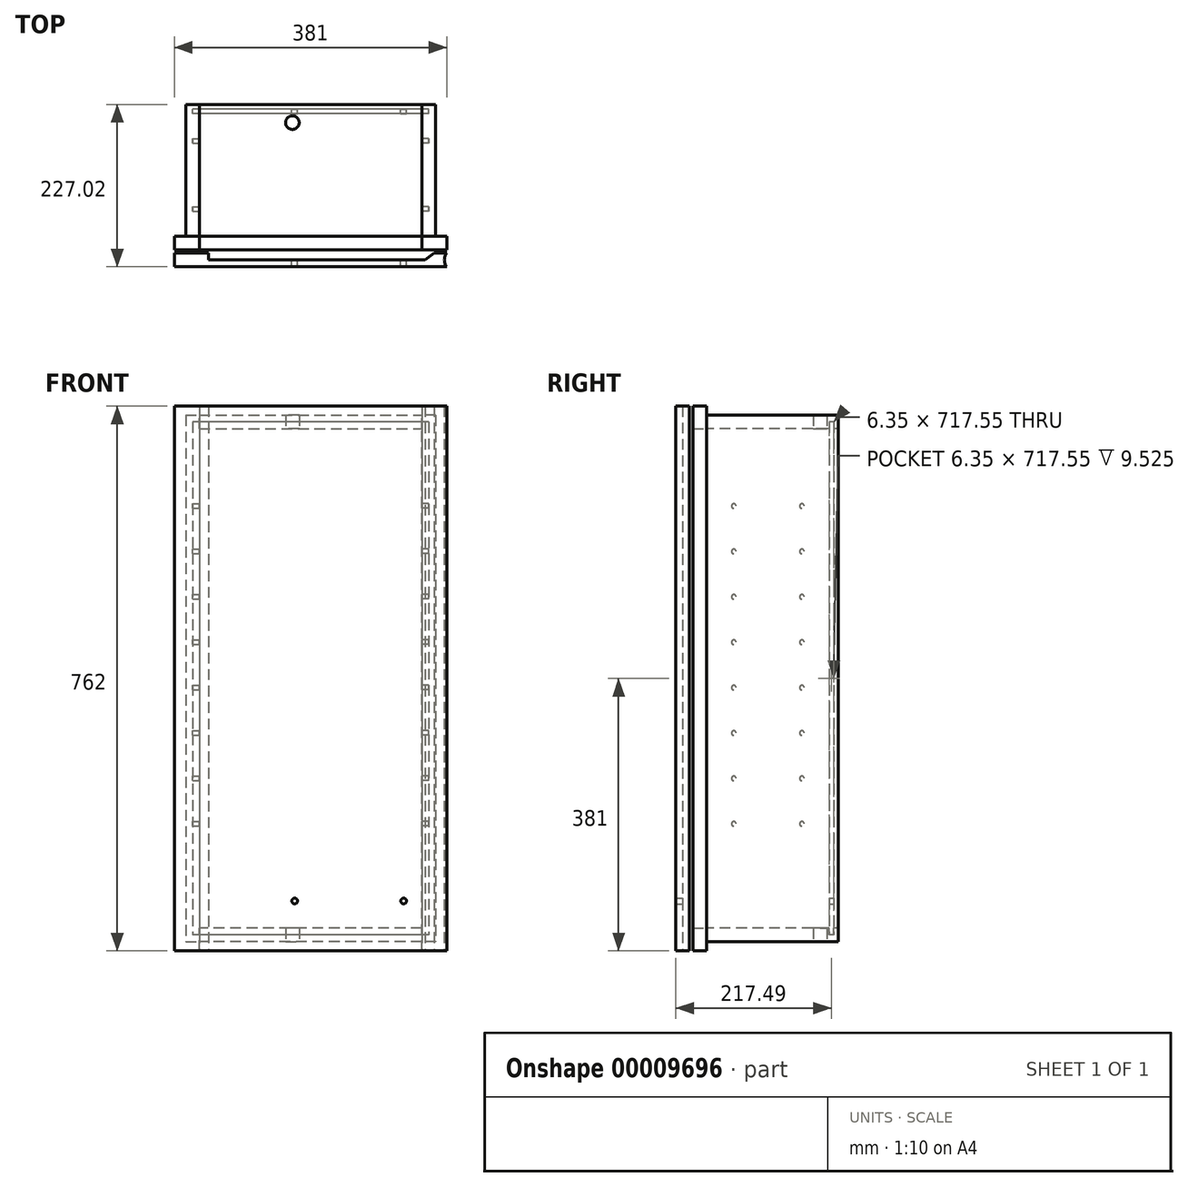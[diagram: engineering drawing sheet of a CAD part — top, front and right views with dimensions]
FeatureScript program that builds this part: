
annotation { "Feature Type Name" : "Feature", "Feature Type Description" : "" }
export const myFeature = defineFeature(function(context is Context, id is Id, definition is map)
    precondition{}
    {
        {
            var Q0;
            Q0=qCreatedBy(makeId("Top.planeOp"),FACE);
            var sketch = newSketch(context, id + "F0", { "sketchPlane" : qUnion([Q0])});
            skLineSegment(sketch, "E0.rect.bottom", {"start": v(155.58, 92.08) * mm, "end": v(-155.58, 92.08) * mm});
            skLineSegment(sketch, "E0.rect.top", {"start": v(155.58, -92.08) * mm, "end": v(-155.58, -92.08) * mm});
            skLineSegment(sketch, "E0.rect.left", {"start": v(155.58, 92.08) * mm, "end": v(155.58, -92.07) * mm});
            skLineSegment(sketch, "E0.rect.right", {"start": v(-155.58, 92.07) * mm, "end": v(-155.58, -92.08) * mm});
            skPoint(sketch, "E0.rect.middle", {"position": v(0, 0) * mm});
            skSolve(sketch);
        }
        {
            var Q0;
            Q0=makeQuery(id+"F0.imprint","IMPRINT",FACE,{"disambiguationData":[TD([[makeQuery(id+"F0.imprint","IMPRINT",EDGE,{"derivedFrom":sQuery(id+"F0.wireOp",EDGE,"E0.rect.bottom")}),1.0]])]});
            extrude(context, id + "F1", {"entities" : qUnion([Q0]), "depth" : 19.05 * mm});
        }
        {
            var Q0;
            Q0=makeQuery(id+"F1.opExtrude","SWEPT_FACE",FACE,{"disambiguationData":[OSD([sQuery(id+"F0.wireOp",EDGE,"E0.rect.right")])]});
            var sketch = newSketch(context, id + "F2", { "sketchPlane" : qUnion([Q0])});
            skLineSegment(sketch, "E1.bottom", {"start": v(-92.07, 0) * mm, "end": v(92.08, 0) * mm});
            skLineSegment(sketch, "E1.top", {"start": v(-92.08, 736.6) * mm, "end": v(92.07, 736.6) * mm});
            skLineSegment(sketch, "E1.left", {"start": v(-92.07, 0) * mm, "end": v(-92.08, 736.6) * mm});
            skLineSegment(sketch, "E1.right", {"start": v(92.08, 0) * mm, "end": v(92.07, 736.6) * mm});
            skSolve(sketch);
        }
        {
            var Q0;
            Q0 = qSketchRegion(id + "F2", true);
            extrude(context, id + "F3", {"entities" : qUnion([Q0]), "depth" : 19.05 * mm});
        }
        {
            var Q0;
            Q0=makeQuery(id+"F3.opExtrude","CAP_FACE",FACE,{"disambiguationData":[OSD([sQuery(id+"F2.wireOp",EDGE,"E1.bottom"),sQuery(id+"F2.wireOp",EDGE,"E1.top"),sQuery(id+"F2.wireOp",EDGE,"E1.left"),sQuery(id+"F2.wireOp",EDGE,"E1.right")])],"isStart":true});
            var sketch = newSketch(context, id + "F4", { "sketchPlane" : qUnion([Q0])});
            skCircle(sketch, "E2", {"center": v(-53.98, 165.1) * mm, "radius": 3.18 * mm});
            skCircle(sketch, "E3", {"center": v(41.27, 165.1) * mm, "radius": 3.18 * mm});
            skLineSegment(sketch, "E4", {"start": v(-53.98, 165.1) * mm, "end": v(41.27, 165.1) * mm, "construction": true});
            skCircle(sketch, "E5.0.1.0", {"center": v(-53.98, 228.6) * mm, "radius": 3.18 * mm});
            skCircle(sketch, "E5.0.1.1", {"center": v(41.27, 228.6) * mm, "radius": 3.18 * mm});
            skCircle(sketch, "E5.0.2.0", {"center": v(-53.98, 292.1) * mm, "radius": 3.18 * mm});
            skCircle(sketch, "E5.0.2.1", {"center": v(41.27, 292.1) * mm, "radius": 3.18 * mm});
            skCircle(sketch, "E5.0.3.0", {"center": v(-53.98, 355.6) * mm, "radius": 3.18 * mm});
            skCircle(sketch, "E5.0.3.1", {"center": v(41.27, 355.6) * mm, "radius": 3.18 * mm});
            skCircle(sketch, "E5.0.4.0", {"center": v(-53.98, 419.1) * mm, "radius": 3.18 * mm});
            skCircle(sketch, "E5.0.4.1", {"center": v(41.27, 419.1) * mm, "radius": 3.18 * mm});
            skCircle(sketch, "E5.0.5.0", {"center": v(-53.98, 482.6) * mm, "radius": 3.18 * mm});
            skCircle(sketch, "E5.0.5.1", {"center": v(41.27, 482.6) * mm, "radius": 3.18 * mm});
            skCircle(sketch, "E5.0.6.0", {"center": v(-53.98, 546.1) * mm, "radius": 3.18 * mm});
            skCircle(sketch, "E5.0.6.1", {"center": v(41.27, 546.1) * mm, "radius": 3.18 * mm});
            skLineSegment(sketch, "E5.direction1", {"start": v(-53.98, 165.1) * mm, "end": v(-25.4, 165.1) * mm, "construction": true});
            skLineSegment(sketch, "E5.direction2", {"start": v(-53.98, 165.1) * mm, "end": v(-53.98, 228.6) * mm, "construction": true});
            skCircle(sketch, "E6.0.0.7", {"center": v(-53.98, 609.6) * mm, "radius": 3.18 * mm});
            skCircle(sketch, "E6.2.0.7", {"center": v(41.27, 609.6) * mm, "radius": 3.18 * mm});
            skLineSegment(sketch, "E7.top", {"start": v(-92.07, 19.05) * mm, "end": v(79.37, 19.05) * mm, "construction": true});
            skLineSegment(sketch, "E7.right", {"start": v(79.37, 736.6) * mm, "end": v(79.37, 19.05) * mm, "construction": true});
            skLineSegment(sketch, "E8", {"start": v(-6.35, 165.1) * mm, "end": v(-6.35, 19.05) * mm, "construction": true});
            skLineSegment(sketch, "E9", {"start": v(79.37, 298.45) * mm, "end": v(-92.08, 298.45) * mm, "construction": true});
            skSolve(sketch);
        }
        {
            var Q0;
            Q0 = qSketchRegion(id + "F4", true);
            extrude(context, id + "F5", {"entities" : qUnion([Q0]), "operationType" : NewBodyOperationType.REMOVE, "oppositeDirection" : true, "depth" : 9.52 * mm});
        }
        {
            var Q0;
            Q0=makeQuery(id+"F3.opExtrude","SWEPT_BODY",BODY,{"disambiguationData":[OSD([sQuery(id+"F2.wireOp",EDGE,"E1.bottom"),sQuery(id+"F2.wireOp",EDGE,"E1.top"),sQuery(id+"F2.wireOp",EDGE,"E1.left"),sQuery(id+"F2.wireOp",EDGE,"E1.right")])]});
            var Q1;
            Q1=qCreatedBy(makeId("Right.planeOp"),FACE);
            mirror(context, id + "F6", {"entities" : qUnion([Q0]), "mirrorPlane" : qUnion([Q1])});
        }
        {
            var Q0;
            Q0=makeQuery(id+"F3.opExtrude","SWEPT_FACE",FACE,{"disambiguationData":[OSD([sQuery(id+"F2.wireOp",EDGE,"E1.top")])]});
            var sketch = newSketch(context, id + "F7", { "sketchPlane" : qUnion([Q0])});
            skLineSegment(sketch, "E10.bottom", {"start": v(-155.58, 92.08) * mm, "end": v(155.58, 92.08) * mm});
            skLineSegment(sketch, "E10.top", {"start": v(-155.58, -92.07) * mm, "end": v(155.58, -92.07) * mm});
            skLineSegment(sketch, "E10.left", {"start": v(-155.58, 92.08) * mm, "end": v(-155.58, -92.07) * mm});
            skLineSegment(sketch, "E10.right", {"start": v(155.58, 92.08) * mm, "end": v(155.58, -92.07) * mm});
            skSolve(sketch);
        }
        {
            var Q0;
            Q0 = qSketchRegion(id + "F7", true);
            extrude(context, id + "F8", {"entities" : qUnion([Q0]), "oppositeDirection" : true, "depth" : 19.05 * mm});
        }
        {
            var Q0;
            Q0=makeQuery(id+"F3.opExtrude","SWEPT_FACE",FACE,{"disambiguationData":[OSD([sQuery(id+"F2.wireOp",EDGE,"E1.left")])]});
            cPlane(context, id + "F9", {"entities" : qUnion([Q0]), "cplaneType" : CPlaneType.OFFSET, "offset" : 6.35 * mm, "oppositeDirection" : true, "width" : 152.4 * mm, "height" : 152.4 * mm});
        }
        {
            var Q0;
            Q0=qCreatedBy(id+"F9.planeOp",FACE);
            var sketch = newSketch(context, id + "F10", { "sketchPlane" : qUnion([Q0])});
            skLineSegment(sketch, "E11.bottom", {"start": v(-165.1, 727.07) * mm, "end": v(165.1, 727.07) * mm});
            skLineSegment(sketch, "E11.top", {"start": v(-165.1, 9.52) * mm, "end": v(165.1, 9.53) * mm});
            skLineSegment(sketch, "E11.left", {"start": v(-165.1, 727.07) * mm, "end": v(-165.1, 9.52) * mm});
            skLineSegment(sketch, "E11.right", {"start": v(165.1, 727.07) * mm, "end": v(165.1, 9.53) * mm});
            skLineSegment(sketch, "E12", {"start": v(0, 9.52) * mm, "end": v(0, 0) * mm});
            skLineSegment(sketch, "E13", {"start": v(-165.1, 368.3) * mm, "end": v(-174.63, 368.3) * mm});
            skSolve(sketch);
        }
        {
            var Q0;
            Q0 = qSketchRegion(id + "F10", true);
            extrude(context, id + "F11", {"entities" : qUnion([Q0]), "operationType" : NewBodyOperationType.REMOVE, "oppositeDirection" : true, "depth" : 6.35 * mm});
        }
        {
            var Q0;
            Q0 = qSketchRegion(id + "F10", true);
            extrude(context, id + "F12", {"entities" : qUnion([Q0]), "oppositeDirection" : true, "depth" : 6.35 * mm});
        }
        {
            var Q0;
            Q0=makeQuery(id+"F3.opExtrude","SWEPT_FACE",FACE,{"disambiguationData":[OSD([sQuery(id+"F2.wireOp",EDGE,"E1.right")])]});
            var sketch = newSketch(context, id + "F13", { "sketchPlane" : qUnion([Q0])});
            skLineSegment(sketch, "E14.bottom", {"start": v(-155.58, 749.3) * mm, "end": v(-190.5, 749.3) * mm});
            skLineSegment(sketch, "E14.left", {"start": v(-155.58, 749.3) * mm, "end": v(-155.58, -12.7) * mm});
            skLineSegment(sketch, "E14.right", {"start": v(-190.5, 749.3) * mm, "end": v(-190.5, -12.7) * mm});
            skLineSegment(sketch, "E15", {"start": v(-190.5, -12.7) * mm, "end": v(-155.58, -12.7) * mm});
            skSolve(sketch);
        }
        {
            var Q0;
            Q0 = qSketchRegion(id + "F13", true);
            extrude(context, id + "F14", {"entities" : qUnion([Q0]), "depth" : 19.05 * mm});
        }
        {
            var Q0;
            Q0=makeQuery(id+"F14.opExtrude","SWEPT_BODY",BODY,{"disambiguationData":[OSD([sQuery(id+"F13.wireOp",EDGE,"E14.bottom"),sQuery(id+"F13.wireOp",EDGE,"E14.left"),sQuery(id+"F13.wireOp",EDGE,"E14.right"),sQuery(id+"F13.wireOp",EDGE,"E15")])]});
            var Q1;
            Q1=qCreatedBy(makeId("Right.planeOp"),FACE);
            mirror(context, id + "F15", {"entities" : qUnion([Q0]), "mirrorPlane" : qUnion([Q1])});
        }
        {
            var Q0;
            Q0=makeQuery(id+"F8.opExtrude","SWEPT_FACE",FACE,{"disambiguationData":[OSD([sQuery(id+"F7.wireOp",EDGE,"E10.top")])]});
            var sketch = newSketch(context, id + "F16", { "sketchPlane" : qUnion([Q0])});
            skLineSegment(sketch, "E16.bottom", {"start": v(-155.58, 749.3) * mm, "end": v(155.58, 749.3) * mm});
            skLineSegment(sketch, "E16.top", {"start": v(-155.58, 717.55) * mm, "end": v(155.58, 717.55) * mm});
            skLineSegment(sketch, "E16.left", {"start": v(-155.58, 749.3) * mm, "end": v(-155.58, 717.55) * mm});
            skLineSegment(sketch, "E16.right", {"start": v(155.58, 749.3) * mm, "end": v(155.58, 717.55) * mm});
            skSolve(sketch);
        }
        {
            var Q0;
            Q0 = qSketchRegion(id + "F16", true);
            extrude(context, id + "F17", {"entities" : qUnion([Q0]), "depth" : 19.05 * mm});
        }
        {
            var Q0;
            {var subQ0=sQuery(id+"F0.wireOp",EDGE,"E0.rect.top");var subQ1=sQuery(id+"F0.wireOp",EDGE,"E0.rect.left");var subQ2=sQuery(id+"F0.wireOp",EDGE,"E0.rect.right");Q0=makeQuery(id+"F11.boolean.opBoolean","SPLIT",FACE,{"disambiguationData":[TD([makeQuery(id+"F1.opExtrude","SWEPT_FACE",FACE,{"disambiguationData":[OSD([subQ0])]})])],"derivedFrom":makeQuery(id+"F1.opExtrude","CAP_FACE",FACE,{"disambiguationData":[OSD([sQuery(id+"F0.wireOp",EDGE,"E0.rect.bottom"),subQ0,subQ1,subQ2])],"isStart":false})});}
            var Q1;
            {var subQ0=sQuery(id+"F7.wireOp",EDGE,"E10.top");var subQ1=sQuery(id+"F7.wireOp",EDGE,"E10.left");var subQ2=sQuery(id+"F7.wireOp",EDGE,"E10.right");Q1=makeQuery(id+"F11.boolean.opBoolean","SPLIT",FACE,{"disambiguationData":[TD([makeQuery(id+"F8.opExtrude","SWEPT_FACE",FACE,{"disambiguationData":[OSD([subQ0])]})])],"derivedFrom":makeQuery(id+"F8.opExtrude","CAP_FACE",FACE,{"disambiguationData":[OSD([sQuery(id+"F7.wireOp",EDGE,"E10.bottom"),subQ0,subQ1,subQ2])],"isStart":false})});}
            cPlane(context, id + "F18", {"entities" : qUnion([Q0, Q1]), "cplaneType" : CPlaneType.MID_PLANE, "offset" : 152.4 * mm, "width" : 152.4 * mm, "height" : 152.4 * mm});
        }
        {
            var Q0;
            Q0=makeQuery(id+"F17.opExtrude","SWEPT_BODY",BODY,{"disambiguationData":[OSD([sQuery(id+"F16.wireOp",EDGE,"E16.bottom"),sQuery(id+"F16.wireOp",EDGE,"E16.top"),sQuery(id+"F16.wireOp",EDGE,"E16.left"),sQuery(id+"F16.wireOp",EDGE,"E16.right")])]});
            var Q1;
            Q1=qCreatedBy(id+"F18.planeOp",FACE);
            mirror(context, id + "F19", {"entities" : qUnion([Q0]), "mirrorPlane" : qUnion([Q1])});
        }
        {
            var Q0;
            Q0=qCreatedBy(id+"F18.planeOp",FACE);
            var sketch = newSketch(context, id + "F20", { "sketchPlane" : qUnion([Q0])});
            skLineSegment(sketch, "E17", {"start": v(-190.5, -115.89) * mm, "end": v(-190.5, -134.94) * mm});
            skLineSegment(sketch, "E18", {"start": v(-190.5, -134.94) * mm, "end": v(190.5, -134.94) * mm});
            skLineSegment(sketch, "E19", {"start": v(-190.5, -115.89) * mm, "end": v(-142.88, -115.89) * mm});
            skLineSegment(sketch, "E20", {"start": v(-142.88, -115.89) * mm, "end": v(-142.88, -125.41) * mm});
            skLineSegment(sketch, "E21", {"start": v(-142.88, -125.41) * mm, "end": v(160.34, -125.41) * mm});
            skLineSegment(sketch, "E22", {"start": v(160.34, -125.41) * mm, "end": v(173.04, -115.89) * mm});
            skLineSegment(sketch, "E23", {"start": v(173.04, -115.89) * mm, "end": v(190.5, -115.89) * mm});
            skArc(sketch, "E24", {"start": v(190.5, -115.89) * mm, "mid": v(187.16, -125.41) * mm, "end": v(190.5, -134.94) * mm});
            skLineSegment(sketch, "E25", {"start": v(0, 0) * mm, "end": v(0, -134.94) * mm, "construction": true});
            skSolve(sketch);
        }
        {
            var Q0;
            Q0 = qSketchRegion(id + "F20", true);
            extrude(context, id + "F21", {"entities" : qUnion([Q0]), "depth" : 762 * mm, "symmetric" : true});
        }
        {
            var Q0;
            Q0=makeQuery(id+"F1.opExtrude","CAP_FACE",FACE,{"disambiguationData":[OSD([sQuery(id+"F0.wireOp",EDGE,"E0.rect.bottom"),sQuery(id+"F0.wireOp",EDGE,"E0.rect.top"),sQuery(id+"F0.wireOp",EDGE,"E0.rect.left"),sQuery(id+"F0.wireOp",EDGE,"E0.rect.right")])],"isStart":true});
            var sketch = newSketch(context, id + "F22", { "sketchPlane" : qUnion([Q0])});
            skCircle(sketch, "E26", {"center": v(-25.4, -66.67) * mm, "radius": 9.53 * mm});
            skSolve(sketch);
        }
        {
            var Q0;
            Q0 = qSketchRegion(id + "F22", true);
            extrude(context, id + "F23", {"entities" : qUnion([Q0]), "operationType" : NewBodyOperationType.REMOVE, "endBound" : BoundingType.THROUGH_ALL, "oppositeDirection" : true, "depth" : 25.4 * mm});
        }
        {
            var Q0;
            Q0=makeQuery(id+"F12.opExtrude","CAP_FACE",FACE,{"disambiguationData":[OSD([sQuery(id+"F10.wireOp",EDGE,"E11.bottom"),sQuery(id+"F10.wireOp",EDGE,"E11.top"),sQuery(id+"F10.wireOp",EDGE,"E11.left"),sQuery(id+"F10.wireOp",EDGE,"E11.right")])],"isStart":true});
            var sketch = newSketch(context, id + "F24", { "sketchPlane" : qUnion([Q0])});
            skCircle(sketch, "E27", {"center": v(-130.18, 57.15) * mm, "radius": 3.97 * mm});
            skCircle(sketch, "E28", {"center": v(22.22, 57.15) * mm, "radius": 3.97 * mm});
            skSolve(sketch);
        }
        {
            var Q0;
            Q0 = qSketchRegion(id + "F24", true);
            extrude(context, id + "F25", {"entities" : qUnion([Q0]), "operationType" : NewBodyOperationType.REMOVE, "endBound" : BoundingType.THROUGH_ALL, "oppositeDirection" : true, "depth" : 25.4 * mm});
        }
    });
